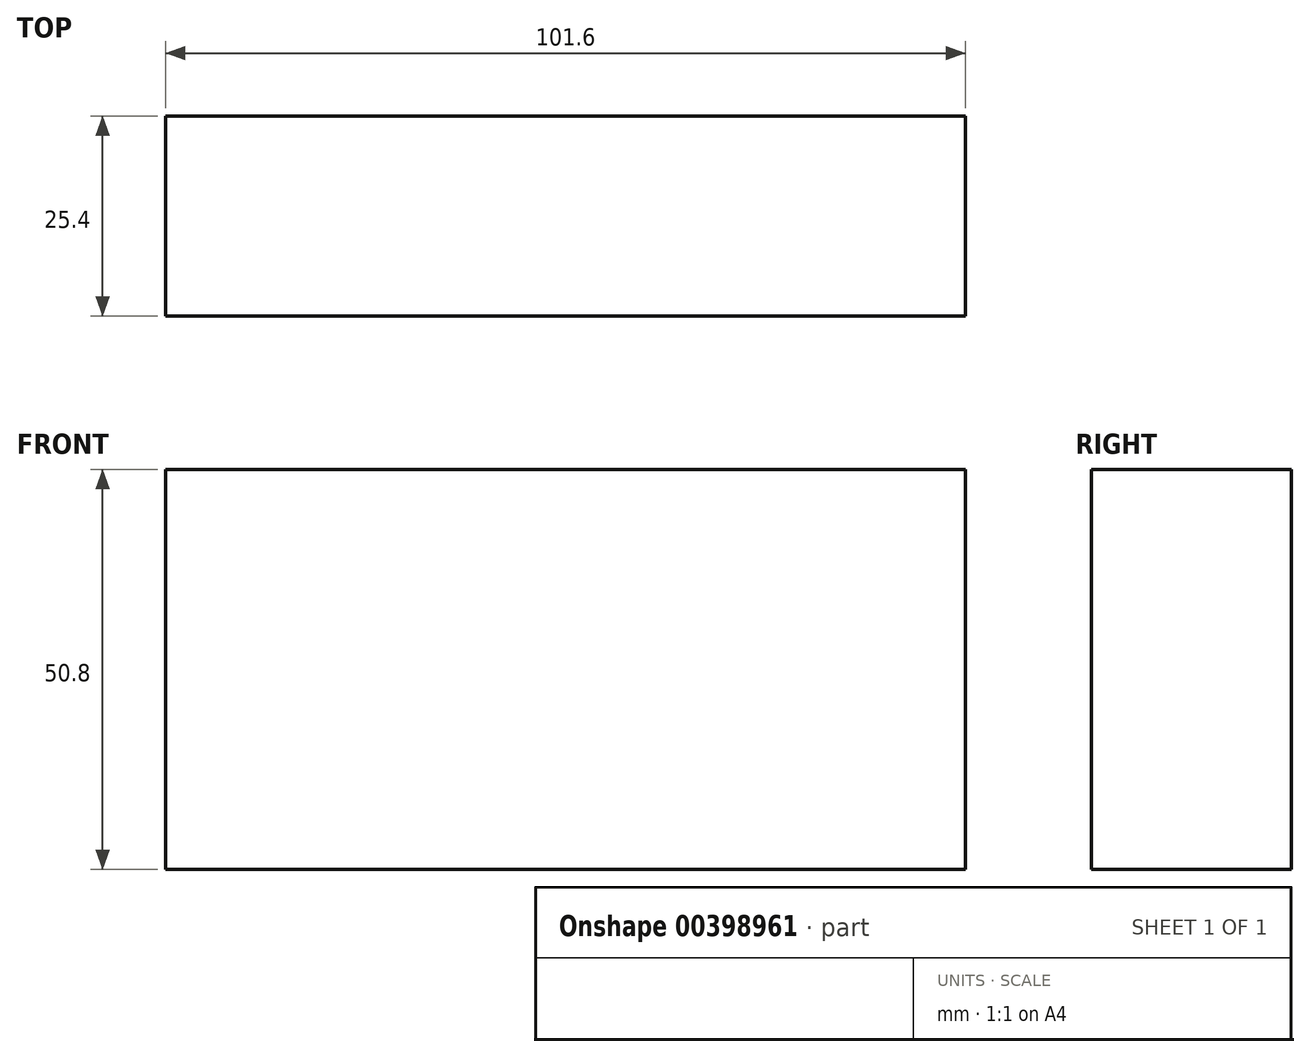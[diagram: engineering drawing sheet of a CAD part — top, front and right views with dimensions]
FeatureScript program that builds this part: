
annotation { "Feature Type Name" : "Feature", "Feature Type Description" : "" }
export const myFeature = defineFeature(function(context is Context, id is Id, definition is map)
    precondition{}
    {
        {
            var Q0;
            Q0=qCreatedBy(makeId("Top.planeOp"),FACE);
            var sketch = newSketch(context, id + "F0", { "sketchPlane" : qUnion([Q0])});
            skLineSegment(sketch, "E0.bottom", {"start": v(50.8, 12.7) * mm, "end": v(-50.8, 12.7) * mm});
            skLineSegment(sketch, "E0.top", {"start": v(50.8, -12.7) * mm, "end": v(-50.8, -12.7) * mm});
            skLineSegment(sketch, "E0.left", {"start": v(50.8, 12.7) * mm, "end": v(50.8, -12.7) * mm});
            skLineSegment(sketch, "E0.right", {"start": v(-50.8, 12.7) * mm, "end": v(-50.8, -12.7) * mm});
            skPoint(sketch, "E0.middle", {"position": v(0, 0) * mm});
            skSolve(sketch);
        }
        {
            var Q0;
            Q0 = qSketchRegion(id + "F0", true);
            extrude(context, id + "F1", {"entities" : qUnion([Q0]), "depth" : 50.8 * mm, "symmetric" : true});
        }
    });
